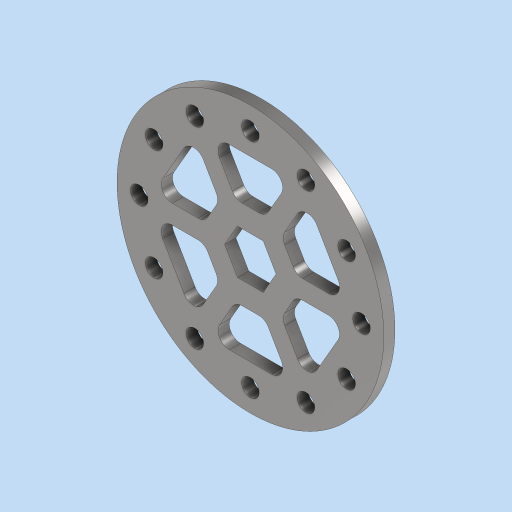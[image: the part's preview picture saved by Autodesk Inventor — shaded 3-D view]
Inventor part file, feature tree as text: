
AUTODESK INVENTOR PART (.ipt)
format: ipt  version: 2023 (Build 270158000, 158)  size: 228,864 bytes
history: native  units: in
note: dims shown in document units (in); Inventor stores cm internally (conversion verified against a paired STEP export)
features: extrude x2, sketch x1, fillet x1, pattern_circular x1
ambient origin geometry x8: Origin, YZ Plane, XZ Plane, XY Plane, X Axis, Y Axis, Z Axis, Center Point
bodies: Solid1 (feature_tree)
feature tree (5):
  sketch  "Sketch1"  dims[d0=3.0in d1=0.5in d2=2.5in d3=0.196in d4=4.7244in d6=360.0deg d8=0.125in d9=0.0in d10=0.125in d11=0.0in d12=0.125in d13=2.3622in d14=360.0deg d16=0.25in d20=0.5in d21=60.0deg d23=0.125in d24=0.125in d25=0.1875in]
  extrude  "Extrusion1"  Depth=0.5in
  extrude  "Extrusion2"  Depth=0.125in
  fillet  "Fillet1"  Radius=0.196in
  pattern_circular  "Circular Pattern1"  Count=12 Angle=360.0deg
